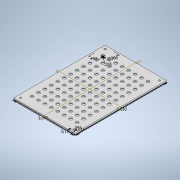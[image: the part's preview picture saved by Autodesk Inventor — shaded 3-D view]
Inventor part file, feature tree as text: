
AUTODESK INVENTOR PART (.ipt)
format: ipt  version: 2020 (Build 240168000, 168)  size: 338,432 bytes
history: native  units: in
note: dims shown in document units (in); Inventor stores cm internally (conversion verified against a paired STEP export)
features: extrude x3, sketch x2, plane x2, mirror x2, hole x1, pattern_linear x1
ambient origin geometry x8: Origin, YZ Plane, XZ Plane, XY Plane, X Axis, Y Axis, Z Axis, Center Point
bodies: Solid1 (feature_tree)
feature tree (11):
  sketch  "Sketch1"  dims[d0=3.365in d1=5.03in]
  extrude  "Extrusion1"  Depth=5.03in
  hole  "Hole1"  [1 undecoded]
  extrude  "Extrusion2"  Depth=0.0787in
  pattern_linear  "Rectangular Pattern1"  Spacing1=0.2756in  [1 undecoded]
  plane  "Work Plane1"
  plane  "Work Plane2"
  extrude  "Extrusion3"  Depth=0.0787in
  mirror  "Mirror1"
  mirror  "Mirror2"
  sketch  "Sketch2"  dims[d2=0.0787in d3=0.0in d4=0.4425in d5=0.5661in d6=0.2756in d7=0.1575in d8=0.75in d9=0.37in d10=0.25in d11=90.0deg d12=0.75in d13=0.0in d14=3.1496in d16=0.3543in d17=4.7244in d19=0.3543in d20=0.1875in d21=0.1875in d29=0.443in d30=0.566in d31=0.2953in d32=0.1575in d33=0.0394in d34=0.0in d35=0.0984in d36=0.0787in d37=0.0in d38=0.0344in]
note: 2 required parameter values undecoded (feature->parameter linkage not recoverable at this tier; creation-order binding heuristic only, values carry confidence <= 0.55)
